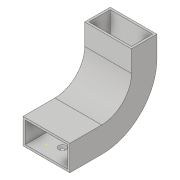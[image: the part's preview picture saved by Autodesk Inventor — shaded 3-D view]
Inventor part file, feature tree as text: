
AUTODESK INVENTOR PART (.ipt)
format: ipt  version: 2018.2 (Build 222227000, 227)  size: 114,176 bytes
history: native  units: in
note: dims shown in document units (in); Inventor stores cm internally (conversion verified against a paired STEP export)
features: sketch x4, sweep x1, extrude x1, chamfer x1
ambient origin geometry x8: Origin, YZ Plane, XZ Plane, XY Plane, X Axis, Y Axis, Z Axis, Center Point
bodies: Solid1 (feature_tree)
feature tree (7):
  sketch  "Sketch1"  dims[d0=3.937in d1=1.9685in]
  sweep  "Sweep1"
  extrude  "Extrusion1"  Depth=2.3622in
  chamfer  "Chamfer1"  [1 undecoded]
  sketch  "Sketch2"  dims[d2=4.3307in d3=2.3622in d7=0.0in d8=0.0in]
  sketch  "Sketch3"  dims[d9=0.2756in]
  sketch  "Sketch4"  dims[d10=0.3937in d11=0.0in d12=0.1969in d13=0.0787in d14=45.0deg]
note: 1 required parameter value undecoded (feature->parameter linkage not recoverable at this tier; creation-order binding heuristic only, values carry confidence <= 0.55)
